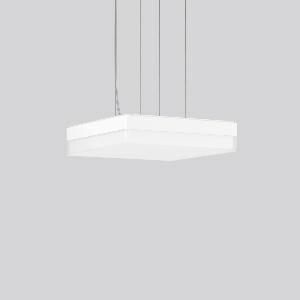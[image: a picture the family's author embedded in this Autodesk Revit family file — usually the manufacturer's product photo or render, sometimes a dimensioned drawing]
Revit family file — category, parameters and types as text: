
# Revit family: flat_slim_square_312541_002_bf27
name_source: partatom
category: Lighting Fixtures
units: mm (PartAtom-declared; Revit-internal decimal feet)

## family parameters
Cut with Voids When Loaded = No
Host = Face
Light Source = No
Part Type = Normal
Room Calculation Point = No
Round Connector Dimension = Use Diameter
Shared = No

## types (1)
- MultiLumen 2 840 (1 x LED Modul 840, 2300 lm, 4000)
    Apparent Load = 19 VA
    CIE Flux Codes = 43 74 93 92 100
    Color Rendering = 80
    Color Temperature = 4000
    Default Elevation = 1800 mm
    Height = 70 mm
    Lamp = 1 x LED Modul 840
    Lamp Light Flux = 2300 lm
    Lamp count = 1
    Length = 300 mm
    Lifetime = 50000 h
    Luminous efficacy = 121 lm/W
    Manufacturer = RZB
    ModVariant = No
    Model = 312541.002
    Mounting Place = Ceiling
    Mounting Type = Pendant
    Number of Poles = 1
    OnlyDefault = Yes
    Power Factor = 1
    Product Name = FLAT SLIM square
    Product group = Pendant luminaires
    ProductGroupID = 902
    Protection Class = Protection class I
    Protection Degree = IP 40
    RLX_Detail_Level = 1
    RLX_Emergency_Light_Flux = 0 lm
    RLX_Emergency_Type = 0
    RLX_Emergency_Type_DB = No
    RlxData = <blob elided: 14213 chars, md5=b6f6c102>
    Socket = socket
    Standby Power = 0 W
    System Light Flux = 2300 lm
    System Power = 19 W
    Type Comments = MultiLumen 2 840
    Type Image = 312541.002.jpg
    URL = http://relux.com
    VarID = multilumen_2_840
    Voltage = 230 V
    Voltage Range = 220-240 V
    Weight = 0.00 kg
    Width = 300 mm

## geometry (parser evidence)
native form markers: Sweep x13
no freeform markers — native parametric forms only
